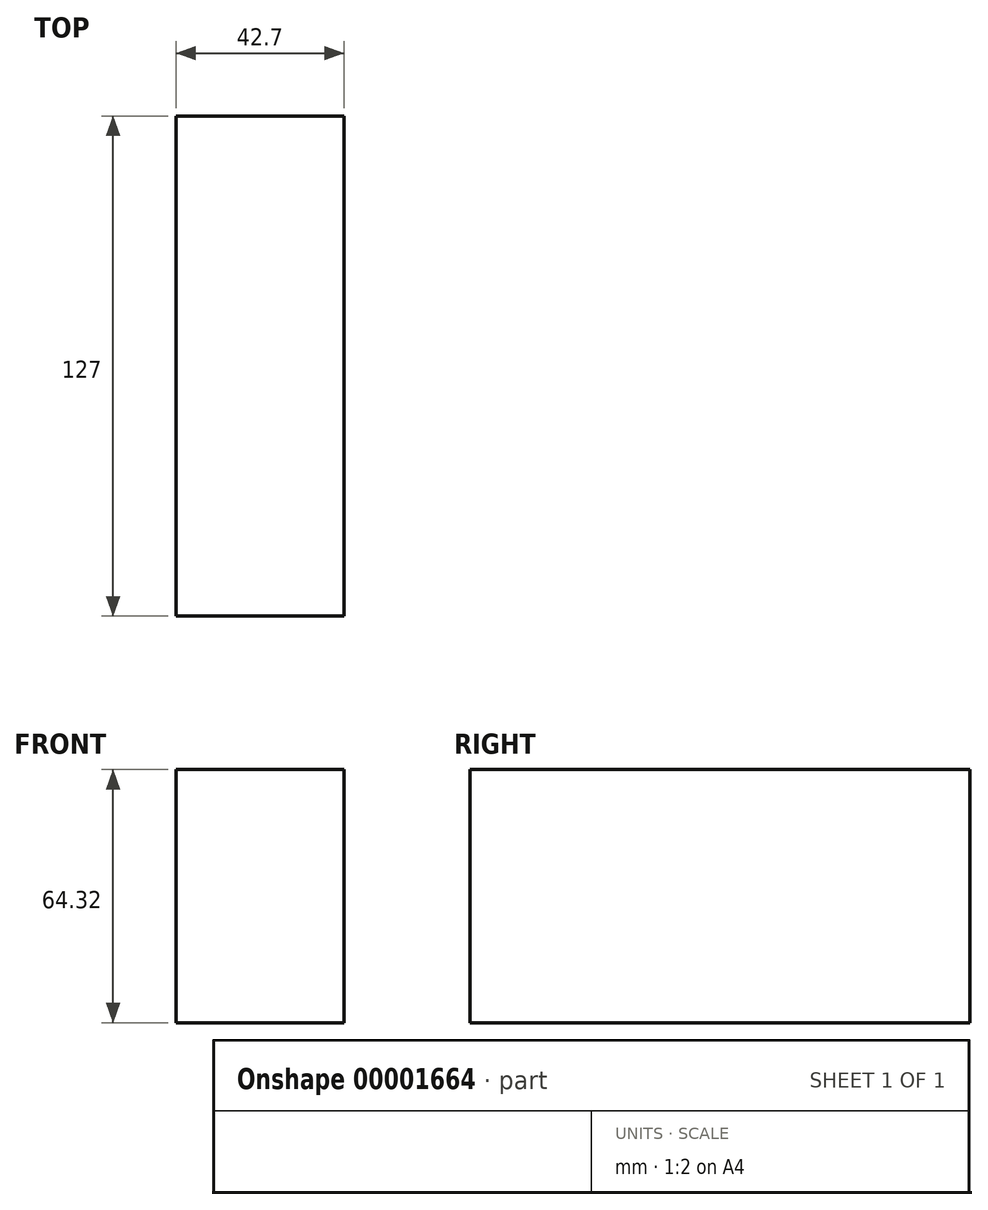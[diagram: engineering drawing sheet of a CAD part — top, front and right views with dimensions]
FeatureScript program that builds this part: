
annotation { "Feature Type Name" : "Feature", "Feature Type Description" : "" }
export const myFeature = defineFeature(function(context is Context, id is Id, definition is map)
    precondition{}
    {
        {
            var Q0;
            Q0=qCreatedBy(makeId("Front.planeOp"),FACE);
            var sketch = newSketch(context, id + "F0", { "sketchPlane" : qUnion([Q0])});
            skLineSegment(sketch, "E0.bottom", {"start": v(-19.15, 39.02) * mm, "end": v(-61.85, 39.02) * mm});
            skLineSegment(sketch, "E0.top", {"start": v(-19.15, -25.3) * mm, "end": v(-61.85, -25.3) * mm});
            skLineSegment(sketch, "E0.left", {"start": v(-19.15, 39.02) * mm, "end": v(-19.15, -25.3) * mm});
            skLineSegment(sketch, "E0.right", {"start": v(-61.85, 39.02) * mm, "end": v(-61.85, -25.3) * mm});
            skSolve(sketch);
        }
        {
            var Q0;
            Q0=makeQuery(id+"F0.imprint","IMPRINT",FACE,{"disambiguationData":[TD([[makeQuery(id+"F0.imprint","IMPRINT",EDGE,{"derivedFrom":sQuery(id+"F0.wireOp",EDGE,"E0.bottom")}),1.0]])]});
            extrude(context, id + "F1", {"entities" : qUnion([Q0]), "depth" : 127 * mm});
        }
    });
